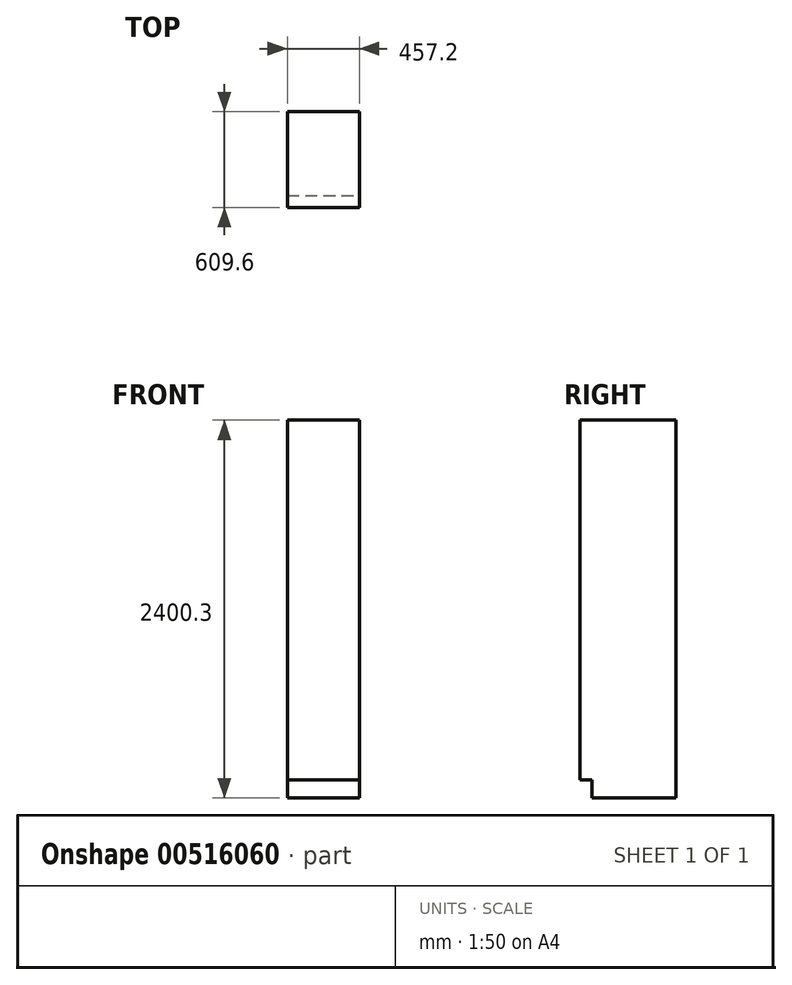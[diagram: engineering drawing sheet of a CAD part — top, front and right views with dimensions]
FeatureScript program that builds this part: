
annotation { "Feature Type Name" : "Feature", "Feature Type Description" : "" }
export const myFeature = defineFeature(function(context is Context, id is Id, definition is map)
    precondition{}
    {
        {
            var Q0;
            Q0=qCreatedBy(makeId("Top.planeOp"),FACE);
            var sketch = newSketch(context, id + "F0", { "sketchPlane" : qUnion([Q0])});
            skLineSegment(sketch, "E0.bottom", {"start": v(228.6, -304.8) * mm, "end": v(-228.6, -304.8) * mm});
            skLineSegment(sketch, "E0.top", {"start": v(228.6, 304.8) * mm, "end": v(-228.6, 304.8) * mm});
            skLineSegment(sketch, "E0.left", {"start": v(228.6, -304.8) * mm, "end": v(228.6, 304.8) * mm});
            skLineSegment(sketch, "E0.right", {"start": v(-228.6, -304.8) * mm, "end": v(-228.6, 304.8) * mm});
            skPoint(sketch, "E0.middle", {"position": v(0, 0) * mm});
            skLineSegment(sketch, "E1", {"start": v(-228.6, -228.6) * mm, "end": v(228.6, -228.6) * mm});
            skSolve(sketch);
        }
        {
            var Q0;
            Q0=makeQuery(id+"F0.imprint","IMPRINT",FACE,{"disambiguationData":[TD([[makeQuery(id+"F0.imprint","IMPRINT",EDGE,{"derivedFrom":sQuery(id+"F0.wireOp",EDGE,"E0.bottom")}),-1.0]])]});
            var Q1;
            {var subQ0=sQuery(id+"F0.wireOp",EDGE,"E0.top");Q1=makeQuery(id+"F0.imprint","IMPRINT",FACE,{"disambiguationData":[TD([[makeQuery(id+"F0.imprint","IMPRINT",EDGE,{"derivedFrom":subQ0}),1.0]])]});}
            extrude(context, id + "F1", {"entities" : qUnion([Q0, Q1]), "depth" : 2286 * mm, "offsetDistance" : 25.4 * mm});
        }
        {
            var Q0;
            {var subQ0=sQuery(id+"F0.wireOp",EDGE,"E0.top");Q0=makeQuery(id+"F0.imprint","IMPRINT",FACE,{"disambiguationData":[TD([[makeQuery(id+"F0.imprint","IMPRINT",EDGE,{"derivedFrom":subQ0}),1.0]])]});}
            extrude(context, id + "F2", {"entities" : qUnion([Q0]), "operationType" : NewBodyOperationType.ADD, "oppositeDirection" : true, "depth" : 114.3 * mm, "offsetDistance" : 25.4 * mm});
        }
    });
